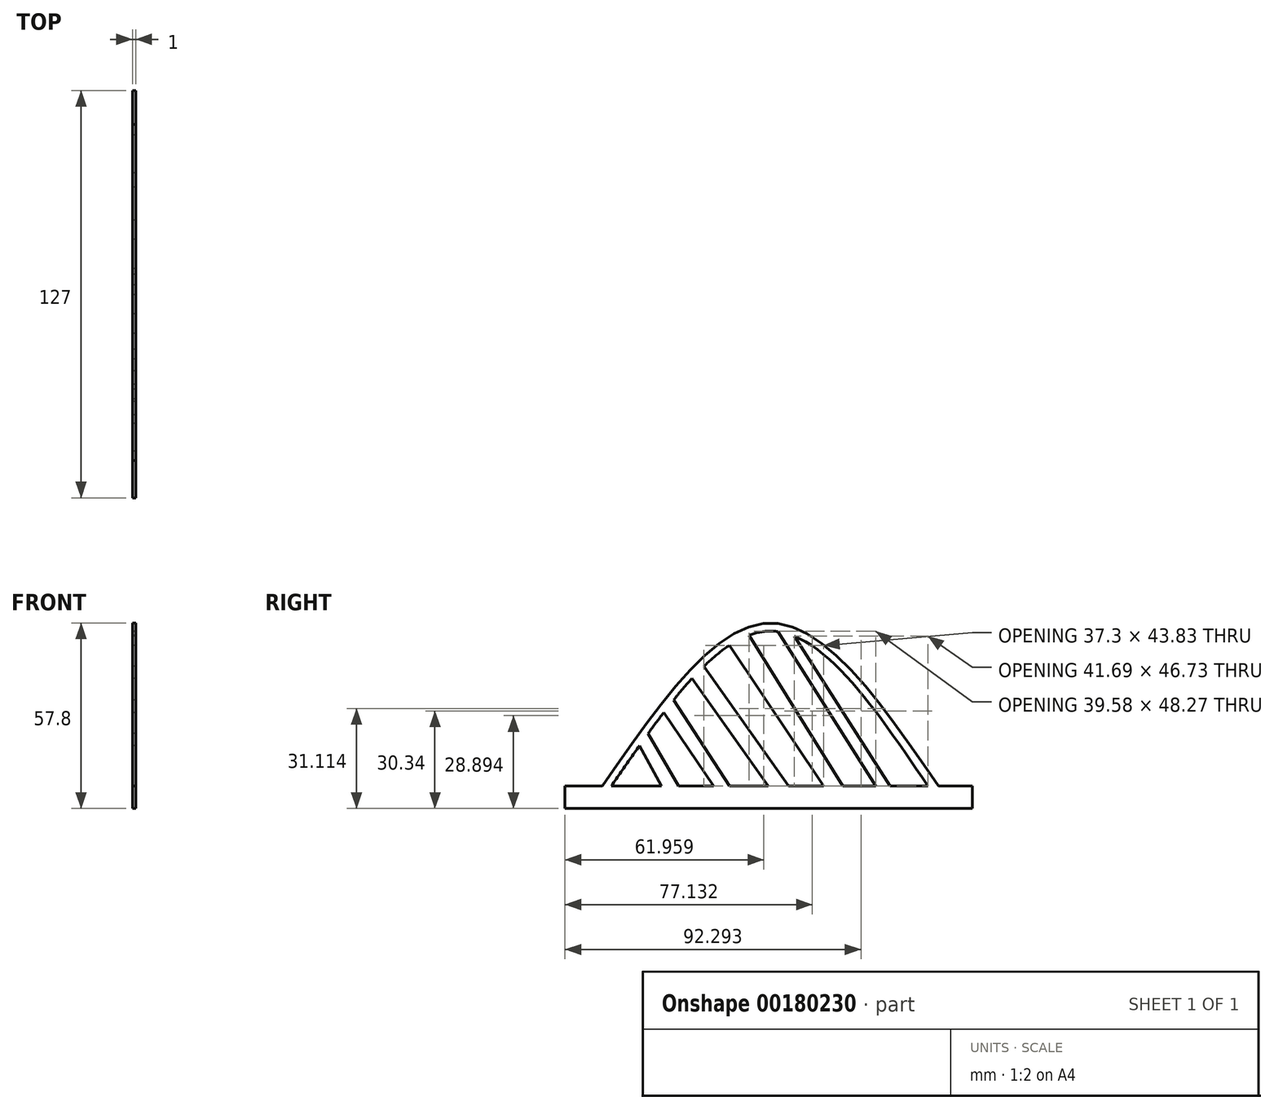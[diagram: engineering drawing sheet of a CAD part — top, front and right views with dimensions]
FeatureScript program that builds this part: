
annotation { "Feature Type Name" : "Feature", "Feature Type Description" : "" }
export const myFeature = defineFeature(function(context is Context, id is Id, definition is map)
    precondition{}
    {
        {
            var Q0;
            Q0=qCreatedBy(makeId("Right.planeOp"),FACE);
            var sketch = newSketch(context, id + "F0", { "sketchPlane" : qUnion([Q0])});
            skLineSegment(sketch, "E0", {"start": v(-64.11, 1.37) * mm, "end": v(-52.42, 1.37) * mm});
            skFitSpline(sketch, "E1", {"points": [v(-52.42, 1.37) * mm, v(0, 52.19) * mm, v(52.33, 1.37) * mm], "startDerivative": vector(104.85, 152.44) * mm, "endDerivative": vector(104.64, -152.47) * mm});
            skFitSpline(sketch, "E2", {"points": [v(-49.6, 1.37) * mm, v(0, 49.64) * mm, v(49.03, 1.37) * mm], "startDerivative": vector(99.25, 144.75) * mm, "endDerivative": vector(97.99, -144.9) * mm});
            skLineSegment(sketch, "E3", {"start": v(-40.9, 13.92) * mm, "end": v(-34.04, 1.37) * mm});
            skLineSegment(sketch, "E4", {"start": v(-38.18, 17.72) * mm, "end": v(-28.66, 1.37) * mm});
            skLineSegment(sketch, "E5", {"start": v(-33.3, 24.28) * mm, "end": v(-17.82, 1.37) * mm});
            skLineSegment(sketch, "E6", {"start": v(-30.27, 28.13) * mm, "end": v(-12.82, 1.37) * mm});
            skLineSegment(sketch, "E7", {"start": v(-24.48, 34.89) * mm, "end": v(-0.8, 1.37) * mm});
            skLineSegment(sketch, "E8", {"start": v(-20.8, 38.67) * mm, "end": v(5.56, 1.37) * mm});
            skLineSegment(sketch, "E9", {"start": v(-12.85, 45.2) * mm, "end": v(16.5, 1.37) * mm});
            skLineSegment(sketch, "E10", {"start": v(-6.77, 48.36) * mm, "end": v(22.44, 1.37) * mm});
            skLineSegment(sketch, "E11", {"start": v(2.3, 49.48) * mm, "end": v(32.81, 1.37) * mm});
            skLineSegment(sketch, "E12", {"start": v(7.34, 48.1) * mm, "end": v(37.24, 1.37) * mm});
            skLineSegment(sketch, "E13.top", {"start": v(-64.11, -5.6) * mm, "end": v(62.89, -5.6) * mm});
            skLineSegment(sketch, "E13.left", {"start": v(-64.11, 1.37) * mm, "end": v(-64.11, -5.6) * mm});
            skLineSegment(sketch, "E13.right", {"start": v(62.89, 1.37) * mm, "end": v(62.89, -5.6) * mm});
            skLineSegment(sketch, "E14.trimOffspring", {"start": v(-49.6, 1.37) * mm, "end": v(-34.04, 1.37) * mm});
            skLineSegment(sketch, "E15.trimOffspring", {"start": v(-12.82, 1.37) * mm, "end": v(-0.8, 1.37) * mm});
            skLineSegment(sketch, "E16", {"start": v(-28.66, 1.37) * mm, "end": v(-17.82, 1.37) * mm});
            skLineSegment(sketch, "E17.trimOffspring", {"start": v(22.44, 1.37) * mm, "end": v(32.81, 1.37) * mm});
            skLineSegment(sketch, "E18.trimOffspring", {"start": v(5.56, 1.37) * mm, "end": v(16.5, 1.37) * mm});
            skLineSegment(sketch, "E19.trimOffspring", {"start": v(37.24, 1.37) * mm, "end": v(49.03, 1.37) * mm});
            skLineSegment(sketch, "E20.trimOffspring", {"start": v(52.33, 1.37) * mm, "end": v(62.51, 1.37) * mm});
            skLineSegment(sketch, "E21.trimOffspring", {"start": v(52.33, 1.37) * mm, "end": v(62.89, 1.37) * mm});
            skSolve(sketch);
        }
        {
            var Q0;
            {var subQ1=sQuery(id+"F0.wireOp",EDGE,"E1");Q0=makeQuery(id+"F0.imprint","IMPRINT",FACE,{"disambiguationData":[TD([[makeQuery(id+"F0.imprint","IMPRINT",EDGE,{"derivedFrom":subQ1}),-1.0]])]});}
            var sketch = newSketch(context, id + "F1", { "sketchPlane" : qUnion([Q0])});
            skSolve(sketch);
        }
        {
            var Q0;
            {var subQ1=sQuery(id+"F0.wireOp",EDGE,"E1");Q0=makeQuery(id+"F1.imprint","IMPRINT",FACE,{"disambiguationData":[TD([[makeQuery(id+"F1.imprint","IMPRINT",EDGE,{"derivedFrom":makeQuery(id+"F0.imprint","IMPRINT",EDGE,{"derivedFrom":subQ1})}),-1.0]])]});}
            extrude(context, id + "F2", {"entities" : qUnion([Q0]), "depth" : mm});
        }
    });
